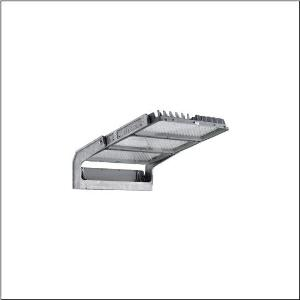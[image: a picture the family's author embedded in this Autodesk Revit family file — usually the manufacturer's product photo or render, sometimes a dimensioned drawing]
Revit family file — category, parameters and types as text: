
# Revit family: floodlight_fl_11_maxi_pro___rs08_5xa779129l01gb_98ff
name_source: partatom
category: Lighting Fixtures
units: mm (PartAtom-declared; Revit-internal decimal feet)

## family parameters
Cut with Voids When Loaded = No
Host = Face
Light Source = No
Part Type = Normal
Room Calculation Point = No
Round Connector Dimension = Use Diameter
Shared = No

## types (1)
- --- (1 x LED, 163120 lm, 1315 W, 5700K)
    Apparent Load = 1315 VA
    CIE Flux Codes = 70 87 98 100 100
    Color Rendering = 70
    Color Temperature = 5700K
    Default Elevation = 1800 mm
    Description = Floodlight FL 11  maxi  pro floodlight; light control with lens of PMMA; cover panel of toughened safety glass, transparent; light distribution: RS08, rotationally symmetric direct distribution, LED; colour temperature: 5700K, rated luminous flux: 163.120lm, colour rendering: CRI > 70, light colour: 757; luminous efficacy: 124lm/W; brightness control: DALI 2; with terminal, 5-pole, max. 2.5mm², mains connection: 220..240V/380..400V AC, 50/60Hz, surge voltage resistance: line to ground: 10kV, LED service life up to 100,000h L90. Typical operating time: 1000h per year., ECG replaceable separately, LED unit replaceable without ESD environment, dustproof LED module, dimming range 10..100%; 1315W floodlight with 3x LED unit of diecast aluminium, coated grey; length: 1.003mm / width: 651mm / height: 338mm; mounting bracket, of diecast aluminium, uncoated, natural, equipment: Power, protection rating (complete): IP66; insulation class (complete): insulation class I (protective earthing); certification: CE, ENEC, VDE; ball protection: ball impact resistant, only for outdoor installations in the designated locations, permissible operating ambient temperature: -45..+55°C, permissible storage temperature: -40..+85°Cpackaging unit: 1 piece

Light Distribution: RS08
    Height = 320 mm
    Lamp = 1 x LED
    Lamp Light Flux = 163120 lm
    Lamp Power = 1315 W
    Lamp count = 1
    Length = 1002 mm
    Luminous efficacy = 124 lm/W
    Manufacturer = Siteco
    ModVariant = No
    Model = 5XA779129L01GB
    Mounting Place = Ceiling
    Mounting Type = Surface mounted
    Number of Poles = 1
    OnlyDefault = Yes
    Power Factor = 1
    Product Name = Floodlight FL 11 maxi pro | RS08
    Product group = floodlight | ceiling mounted
    ProductGroupID = 303
    Protection Class = Protection class I
    Protection Degree = IP 66
    RLX_Detail_Level = 1
    RLX_Emergency_Light_Flux = 0 lm
    RLX_Emergency_Type = 0
    RLX_Emergency_Type_DB = No
    RlxData = <blob elided: 40121 chars, md5=940db30e>
    Socket = socket
    Standby Power = 0 W
    System Light Flux = 163120 lm
    System Power = 1315 W
    Type Comments = factory setting: luminous flux: 100 % | dim-lin: 254 | 895 mA
    Type Image = l_1356210.jpg
    URL = http://relux.com
    VarID = @adj_040145
    Voltage = 0 V
    Weight = 0.00 kg
    Width = 655 mm

## geometry (parser evidence)
native form markers: Blend x4, Sweep x15
no freeform markers — native parametric forms only
